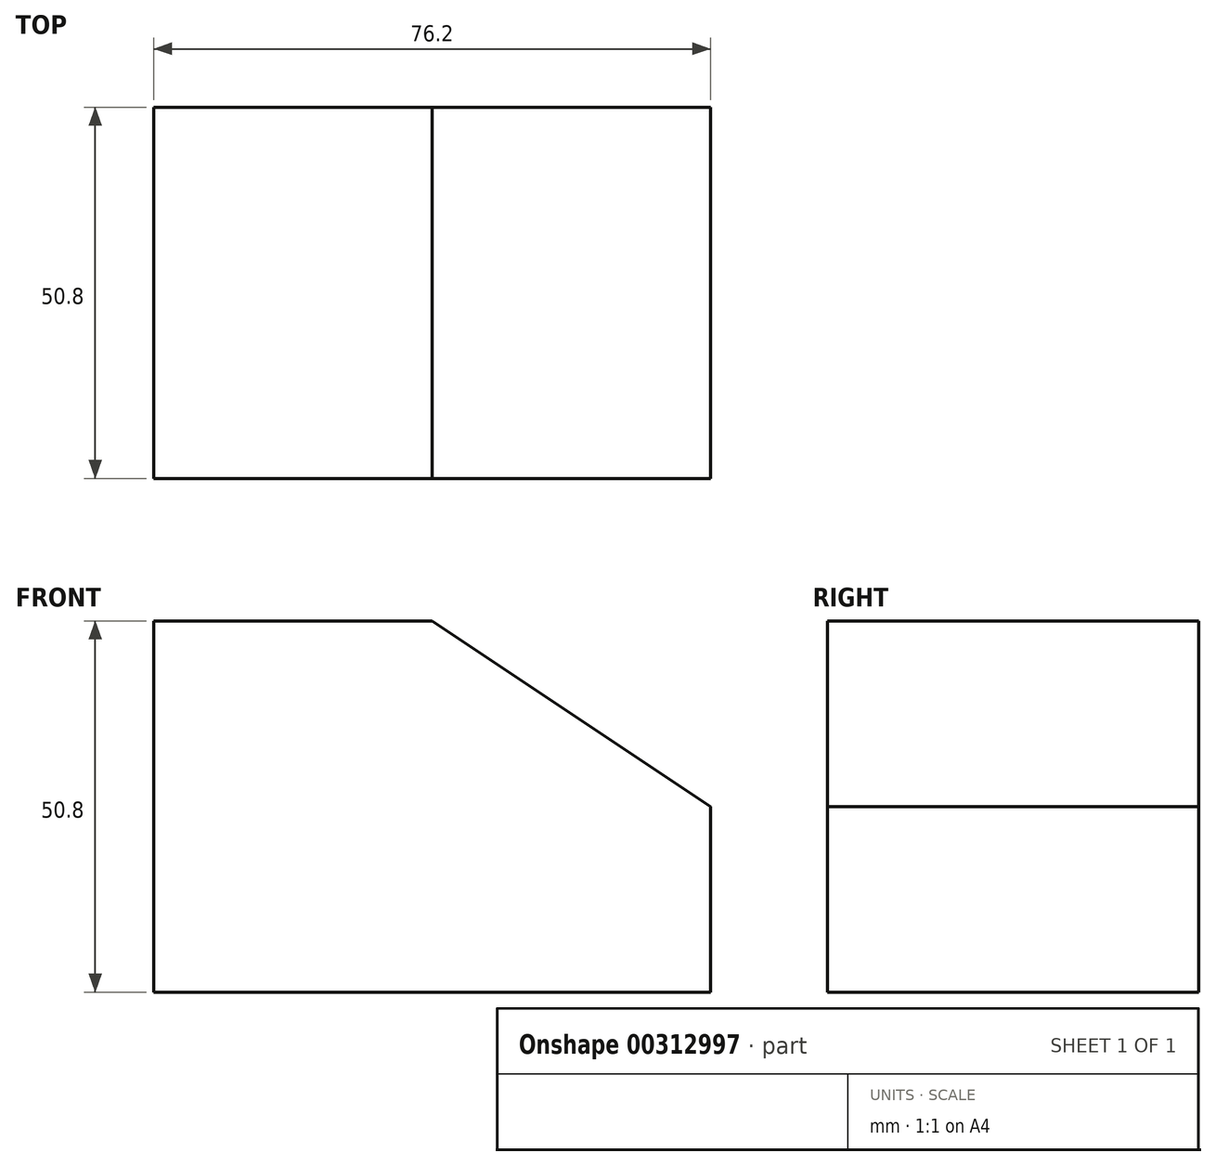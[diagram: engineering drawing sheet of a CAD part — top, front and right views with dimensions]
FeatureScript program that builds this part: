
annotation { "Feature Type Name" : "Feature", "Feature Type Description" : "" }
export const myFeature = defineFeature(function(context is Context, id is Id, definition is map)
    precondition{}
    {
        {
            var Q0;
            Q0=qCreatedBy(makeId("Front.planeOp"),FACE);
            var sketch = newSketch(context, id + "F0", { "sketchPlane" : qUnion([Q0])});
            skLineSegment(sketch, "E0", {"start": v(-16.28, -26.03) * mm, "end": v(59.92, -26.03) * mm});
            skLineSegment(sketch, "E1", {"start": v(59.92, -26.03) * mm, "end": v(59.92, -0.63) * mm});
            skLineSegment(sketch, "E2", {"start": v(59.92, -0.63) * mm, "end": v(21.82, 24.77) * mm});
            skLineSegment(sketch, "E3", {"start": v(21.82, 24.77) * mm, "end": v(-16.28, 24.77) * mm});
            skLineSegment(sketch, "E4", {"start": v(-16.28, 24.77) * mm, "end": v(-16.28, -26.03) * mm});
            skSolve(sketch);
        }
        {
            var Q0;
            Q0=makeQuery(id+"F0.imprint","IMPRINT",FACE,{"disambiguationData":[TD([[makeQuery(id+"F0.imprint","IMPRINT",EDGE,{"derivedFrom":sQuery(id+"F0.wireOp",EDGE,"E0")}),1.0]])]});
            extrude(context, id + "F1", {"entities" : qUnion([Q0]), "oppositeDirection" : true, "depth" : 50.8 * mm});
        }
    });
